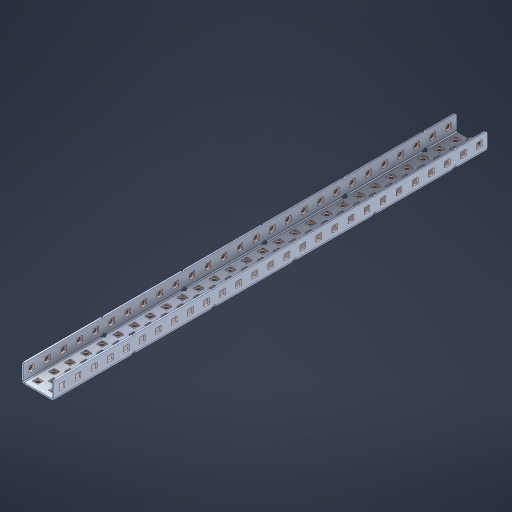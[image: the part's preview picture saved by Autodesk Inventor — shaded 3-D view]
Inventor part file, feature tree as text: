
AUTODESK INVENTOR PART (.ipt)
format: ipt  version: 2023 (Build 270158000, 158)  size: 1,731,072 bytes
history: native  units: in
note: dims shown in document units (in); Inventor stores cm internally (conversion verified against a paired STEP export)
features: other x142, extrude x133, sheet_metal_op x11, sketch x10, pattern_linear x2, mirror x1, chamfer x1
ambient origin geometry x8: Origin, YZ Plane, XZ Plane, XY Plane, X Axis, Y Axis, Z Axis, Center Point
bodies: Solid1 (feature_tree), Body (feature_tree)
feature tree (300):
  sheet_metal_op  "Flanges"
  other  "Flange Pattern Plane"
  other  "Flange Pattern Sketch"
  sheet_metal_op  "Flange Pattern"
  sheet_metal_op  "Body Pattern"
  pattern_linear  "Center Pattern"  Spacing1=0.0469in  [1 undecoded]
  other  "Arc Length"
  mirror  "Notch Mirror"
  pattern_linear  "Notch Pattern"  Spacing1=0.182in  [1 undecoded]
  chamfer  "End Chamfer"
  extrude  "Half Cut"  Depth=0.02in
  sketch  "Sketch1"  dims[d0=1.0in]
  other  "Plate1"
  sketch  "Sketch2"  dims[d1=13.5in]
  other  "Plate2"
  sheet_metal_op  "Bend1"
  sheet_metal_op  "Corner1"
  sketch  "Sketch3"  dims[d2=0.0469in]
  sketch  "Sketch7"  dims[d3=0.0469in]
  other  "Srf1"
  other  "Srf2"
  sketch  "Sketch8"  dims[d4=0.0234in]
  sketch  "Sketch9"  dims[d5=0.0938in]
  other  "Srf91"
  sheet_metal_op  "Body Pattern Sketch"
  other  "Srf92"
  sketch  "Sketch13"  dims[d6=0.0469in]
  sketch  "Sketch14"  dims[d7=0.5in d8=90.0deg d9=0.0312in]
  sketch  "Sketch15"  dims[d10=0.1875in]
  sketch  "Sketch16"  dims[d11=0.0469in d12=0.0469in d16=0.182in d17=0.02in d18=0.0469in d19=0.0in d20=0.25in d21=0.25in d38=10.6299in d40=0.5in d41=0.7874in d43=1.0in d46=0.172in d47=1.0in d48=0.0in d49=0.182in d50=0.02in d51=0.25in d52=0.25in d53=0.0469in d54=0.0in d55=0.172in d56=1.0in d57=0.0in d58=0.25in d60=10.6299in d62=0.5in d63=0.7874in d65=0.5in d85=0.1227in d86=0.1659in d88=0.04in d89=0.0469in d90=0.0in d91=0.04in d92=0.0491in d95=2.5in d96=0.04in d97=0.25in d98=45.0deg d99=0.25in d100=0.5in d101=0.0in d102=2.497in d106=0.182in d107=0.02in d108=0.5in d109=0.5in d110=0.0469in d111=0.0in d112=0.172in d113=0.5in d114=0.0in d117=0.5in d118=0.5in d119=0.5in]
  other  "Srf786"
  other  "Srf823"
  other  "Srf824"
  other  "Srf825"
  other  "Srf826"
  other  "Srf827"
  other  "Srf828"
  other  "Srf829"
  other  "Srf856"
  other  "Srf857"
  other  "Srf858"
  other  "Srf859"
  other  "Srf860"
  other  "Srf861"
  other  "Srf862"
  other  "Srf889"
  other  "Srf890"
  other  "Srf891"
  other  "Srf892"
  other  "Srf893"
  other  "Srf894"
  other  "Srf895"
  other  "Srf896"
  other  "Srf922"
  other  "Srf923"
  other  "Srf924"
  other  "Srf925"
  other  "Srf926"
  other  "Srf959"
  other  "Srf960"
  other  "Srf961"
  other  "Srf962"
  other  "Srf963"
  other  "Srf996"
  other  "Srf997"
  other  "Srf998"
  other  "Srf999"
  other  "Srf1000"
  other  "Srf1143"
  other  "Srf1144"
  other  "Srf1145"
  other  "Srf1146"
  other  "Srf1147"
  other  "Srf1148"
  other  "Srf1149"
  other  "Srf1150"
  other  "Srf1151"
  other  "Srf1152"
  other  "Srf1153"
  other  "Srf1154"
  other  "Srf1155"
  other  "Srf1156"
  other  "Srf1157"
  other  "Srf1158"
  other  "Srf1159"
  other  "Srf1160"
  other  "Srf1161"
  other  "Srf1162"
  other  "Srf1163"
  other  "Srf1164"
  other  "Srf1165"
  other  "Srf1166"
  other  "Srf1167"
  other  "Srf1168"
  other  "Srf1169"
  other  "Srf1170"
  other  "Srf1171"
  other  "Srf1172"
  other  "Srf1173"
  other  "Srf1174"
  other  "Srf1175"
  other  "Srf1176"
  other  "Srf1177"
  other  "Srf1178"
  other  "Srf1179"
  other  "Srf1180"
  other  "Srf1181"
  other  "Srf1182"
  other  "Srf1199"
  other  "Srf1200"
  other  "Srf1201"
  other  "Srf1202"
  other  "Srf1203"
  other  "Srf1204"
  other  "Srf1205"
  other  "Srf1206"
  other  "Srf1207"
  other  "Srf1208"
  other  "Srf1209"
  other  "Srf1210"
  other  "Srf1211"
  other  "Srf1212"
  other  "Srf1213"
  other  "Srf1214"
  other  "Srf1215"
  other  "Srf1216"
  other  "Srf1217"
  other  "Srf1218"
  other  "Srf1219"
  other  "Srf1220"
  other  "Srf1221"
  other  "Srf1222"
  other  "Srf1223"
  other  "Srf1224"
  other  "Srf1225"
  other  "Srf1226"
  other  "Srf1227"
  other  "Srf1228"
  other  "Srf1229"
  other  "Srf1230"
  other  "Srf1231"
  other  "Srf1232"
  other  "Srf1233"
  other  "Srf1234"
  other  "Srf1235"
  other  "Srf1236"
  other  "Srf1237"
  other  "Srf1238"
  other  "Srf1255"
  other  "Srf1256"
  other  "Srf1257"
  other  "Srf1258"
  other  "Srf1259"
  other  "Srf1260"
  other  "Srf1261"
  other  "Srf1262"
  other  "Srf1263"
  other  "Srf1264"
  other  "Srf1265"
  other  "Srf1266"
  other  "Srf1267"
  sheet_metal_op  "Flange Stamp"
  sheet_metal_op  "Flange Circle"
  sheet_metal_op  "Body Stamp"
  sheet_metal_op  "Body Circle"
  other  "Center Stamp"
  other  "Center Circle"
  sheet_metal_op  "Notch"
  extrude  "ExtrusionSrf2"  Depth=0.0469in
  extrude  "ExtrusionSrf92"  TaperAngle=0.0deg  [1 undecoded]
  extrude  "ExtrusionSrf823"  Depth=0.5in
  extrude  "ExtrusionSrf824"  Depth=0.5in
  extrude  "ExtrusionSrf825"  Depth=0.5in
  extrude  "ExtrusionSrf826"  Depth=0.5in
  extrude  "ExtrusionSrf827"  Depth=1.0in TaperAngle=0.0deg
  extrude  "ExtrusionSrf828"  Depth=0.5in
  extrude  "ExtrusionSrf829"  Depth=0.02in
  extrude  "ExtrusionSrf856"  Depth=0.5in
  extrude  "ExtrusionSrf857"  Depth=0.5in
  extrude  "ExtrusionSrf858"  Depth=0.0469in
  extrude  "ExtrusionSrf859"  TaperAngle=0.0deg  [1 undecoded]
  extrude  "ExtrusionSrf860"  Depth=0.5in
  extrude  "ExtrusionSrf861"  Depth=1.0in TaperAngle=0.0deg
  extrude  "ExtrusionSrf862"  Depth=0.5in
  extrude  "ExtrusionSrf889"  Depth=0.5in
  extrude  "ExtrusionSrf890"  Depth=0.5in
  extrude  "ExtrusionSrf891"  Depth=0.5in
  extrude  "ExtrusionSrf892"  Depth=0.5in
  extrude  "ExtrusionSrf893"  Depth=0.5in
  extrude  "ExtrusionSrf894"  Depth=0.0469in
  extrude  "ExtrusionSrf895"  TaperAngle=0.0deg  [1 undecoded]
  extrude  "ExtrusionSrf896"  Depth=0.5in
  extrude  "ExtrusionSrf922"  Depth=0.5in
  extrude  "ExtrusionSrf923"  Depth=2.5in
  extrude  "ExtrusionSrf924"  Depth=0.5in TaperAngle=45.0deg
  extrude  "ExtrusionSrf925"  Depth=0.5in
  extrude  "ExtrusionSrf926"  Depth=0.5in TaperAngle=0.0deg
  extrude  "ExtrusionSrf959"  Depth=0.5in
  extrude  "ExtrusionSrf960"  Depth=0.5in
  extrude  "ExtrusionSrf961"  Depth=0.02in
  extrude  "ExtrusionSrf962"  Depth=0.5in
  extrude  "ExtrusionSrf963"  Depth=0.5in
  extrude  "ExtrusionSrf996"  Depth=0.0469in
  extrude  "ExtrusionSrf997"  TaperAngle=0.0deg  [1 undecoded]
  extrude  "ExtrusionSrf998"  Depth=0.5in
  extrude  "ExtrusionSrf999"  Depth=0.5in TaperAngle=0.0deg
  extrude  "ExtrusionSrf1000"  Depth=0.5in
  extrude  "ExtrusionSrf1143"  Depth=0.5in
  extrude  "ExtrusionSrf1144"  Depth=0.5in
  extrude  "ExtrusionSrf1145"  [1 undecoded]
  extrude  "ExtrusionSrf1146"  [1 undecoded]
  extrude  "ExtrusionSrf1147"  [1 undecoded]
  extrude  "ExtrusionSrf1148"  [1 undecoded]
  extrude  "ExtrusionSrf1149"  [1 undecoded]
  extrude  "ExtrusionSrf1150"  [1 undecoded]
  extrude  "ExtrusionSrf1151"  [1 undecoded]
  extrude  "ExtrusionSrf1152"  [1 undecoded]
  extrude  "ExtrusionSrf1153"  [1 undecoded]
  extrude  "ExtrusionSrf1154"  [1 undecoded]
  extrude  "ExtrusionSrf1155"  [1 undecoded]
  extrude  "ExtrusionSrf1156"  [1 undecoded]
  extrude  "ExtrusionSrf1157"  [1 undecoded]
  extrude  "ExtrusionSrf1158"  [1 undecoded]
  extrude  "ExtrusionSrf1159"  [1 undecoded]
  extrude  "ExtrusionSrf1160"  [1 undecoded]
  extrude  "ExtrusionSrf1161"  [1 undecoded]
  extrude  "ExtrusionSrf1162"  [1 undecoded]
  extrude  "ExtrusionSrf1163"  [1 undecoded]
  extrude  "ExtrusionSrf1164"  [1 undecoded]
  extrude  "ExtrusionSrf1165"  [1 undecoded]
  extrude  "ExtrusionSrf1166"  [1 undecoded]
  extrude  "ExtrusionSrf1167"  [1 undecoded]
  extrude  "ExtrusionSrf1168"  [1 undecoded]
  extrude  "ExtrusionSrf1169"  [1 undecoded]
  extrude  "ExtrusionSrf1170"  [1 undecoded]
  extrude  "ExtrusionSrf1171"  [1 undecoded]
  extrude  "ExtrusionSrf1172"  [1 undecoded]
  extrude  "ExtrusionSrf1173"  [1 undecoded]
  extrude  "ExtrusionSrf1174"  [1 undecoded]
  extrude  "ExtrusionSrf1175"  [1 undecoded]
  extrude  "ExtrusionSrf1176"  [1 undecoded]
  extrude  "ExtrusionSrf1177"  [1 undecoded]
  extrude  "ExtrusionSrf1178"  [1 undecoded]
  extrude  "ExtrusionSrf1179"  [1 undecoded]
  extrude  "ExtrusionSrf1180"  [1 undecoded]
  extrude  "ExtrusionSrf1181"  [1 undecoded]
  extrude  "ExtrusionSrf1182"  [1 undecoded]
  extrude  "ExtrusionSrf1199"  [1 undecoded]
  extrude  "ExtrusionSrf1200"  [1 undecoded]
  extrude  "ExtrusionSrf1201"  [1 undecoded]
  extrude  "ExtrusionSrf1202"  [1 undecoded]
  extrude  "ExtrusionSrf1203"  [1 undecoded]
  extrude  "ExtrusionSrf1204"  [1 undecoded]
  extrude  "ExtrusionSrf1205"  [1 undecoded]
  extrude  "ExtrusionSrf1206"  [1 undecoded]
  extrude  "ExtrusionSrf1207"  [1 undecoded]
  extrude  "ExtrusionSrf1208"  [1 undecoded]
  extrude  "ExtrusionSrf1209"  [1 undecoded]
  extrude  "ExtrusionSrf1210"  [1 undecoded]
  extrude  "ExtrusionSrf1211"  [1 undecoded]
  extrude  "ExtrusionSrf1212"  [1 undecoded]
  extrude  "ExtrusionSrf1213"  [1 undecoded]
  extrude  "ExtrusionSrf1214"  [1 undecoded]
  extrude  "ExtrusionSrf1215"  [1 undecoded]
  extrude  "ExtrusionSrf1216"  [1 undecoded]
  extrude  "ExtrusionSrf1217"  [1 undecoded]
  extrude  "ExtrusionSrf1218"  [1 undecoded]
  extrude  "ExtrusionSrf1219"  [1 undecoded]
  extrude  "ExtrusionSrf1220"  [1 undecoded]
  extrude  "ExtrusionSrf1221"  [1 undecoded]
  extrude  "ExtrusionSrf1222"  [1 undecoded]
  extrude  "ExtrusionSrf1223"  [1 undecoded]
  extrude  "ExtrusionSrf1224"  [1 undecoded]
  extrude  "ExtrusionSrf1225"  [1 undecoded]
  extrude  "ExtrusionSrf1226"  [1 undecoded]
  extrude  "ExtrusionSrf1227"  [1 undecoded]
  extrude  "ExtrusionSrf1228"  [1 undecoded]
  extrude  "ExtrusionSrf1229"  [1 undecoded]
  extrude  "ExtrusionSrf1230"  [1 undecoded]
  extrude  "ExtrusionSrf1231"  [1 undecoded]
  extrude  "ExtrusionSrf1232"  [1 undecoded]
  extrude  "ExtrusionSrf1233"  [1 undecoded]
  extrude  "ExtrusionSrf1234"  [1 undecoded]
  extrude  "ExtrusionSrf1235"  [1 undecoded]
  extrude  "ExtrusionSrf1236"  [1 undecoded]
  extrude  "ExtrusionSrf1237"  [1 undecoded]
  extrude  "ExtrusionSrf1238"  [1 undecoded]
  extrude  "ExtrusionSrf1255"  [1 undecoded]
  extrude  "ExtrusionSrf1256"  [1 undecoded]
  extrude  "ExtrusionSrf1257"  [1 undecoded]
  extrude  "ExtrusionSrf1258"  [1 undecoded]
  extrude  "ExtrusionSrf1259"  [1 undecoded]
  extrude  "ExtrusionSrf1260"  [1 undecoded]
  extrude  "ExtrusionSrf1261"  [1 undecoded]
  extrude  "ExtrusionSrf1262"  [1 undecoded]
  extrude  "ExtrusionSrf1263"  [1 undecoded]
  extrude  "ExtrusionSrf1264"  [1 undecoded]
  extrude  "ExtrusionSrf1265"  [1 undecoded]
  extrude  "ExtrusionSrf1266"  [1 undecoded]
  extrude  "ExtrusionSrf1267"  [1 undecoded]
note: 97 required parameter values undecoded (feature->parameter linkage not recoverable at this tier; creation-order binding heuristic only, values carry confidence <= 0.55)
